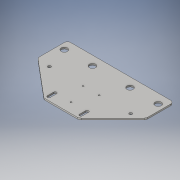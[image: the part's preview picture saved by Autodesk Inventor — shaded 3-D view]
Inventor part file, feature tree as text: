
AUTODESK INVENTOR PART (.ipt)
format: ipt  version: 2016 (Build 200138000, 138)  size: 213,504 bytes
history: native  units: in
note: dims shown in document units (in); Inventor stores cm internally (conversion verified against a paired STEP export)
features: sketch x7, extrude x4, hole x3
ambient origin geometry x8: Origin, YZ Plane, XZ Plane, XY Plane, X Axis, Y Axis, Z Axis, Center Point
bodies: Solid1 (feature_tree)
feature tree (14):
  extrude  "Extrusion1"  Depth=8.5in
  hole  "Hole1"  [1 undecoded]
  extrude  "Extrusion3"  Depth=3.1102in
  extrude  "Extrusion4"  Depth=0.25in
  extrude  "Extrusion5"  Depth=1.0236in
  hole  "Hole3"  [1 undecoded]
  hole  "Hole2"  [1 undecoded]
  sketch  "Sketch1"  dims[d0=8.5in d1=6.0in]
  sketch  "Sketch2"  dims[d2=0.125in d3=0.0in d4=5.6831in]
  sketch  "Sketch3"  dims[d5=1.0236in d7=3.1102in]
  sketch  "Sketch5"  dims[d12=0.2362in d13=0.75in d14=0.375in d15=0.25in d16=0.5635in d17=1.0in d18=0.8108in d19=1.0768in]
  sketch  "Sketch7"  dims[d20=3.1102in d21=1.0236in]
  sketch  "Sketch8"  dims[d22=3.124in d23=7.5728in]
  sketch  "Sketch10"  dims[d24=0.2953in d40=3.8881in d43=1.0in d44=0.0in d45=1.75in d47=1.75in d48=1.75in d49=1.75in d50=2.382in d52=2.5591in d53=0.6398in d54=0.6398in d55=2.382in d58=2.0472in d62=1.2795in d64=0.1181in d65=0.75in d66=0.375in d67=0.25in d68=0.5635in d69=1.0in d70=0.8108in d72=0.2362in d76=0.236in d77=0.492in d78=0.236in d79=0.492in d80=1.0in d81=0.0in d82=0.236in d83=0.492in d84=0.236in d85=0.492in d86=1.0in d87=0.0in d88=0.2362in d93=0.2953in d96=2.07in d99=135.0deg d100=0.25in d101=0.25in d102=0.25in d103=0.25in d104=0.962in d110=0.5in d111=2.25in d112=3.0in d113=2.25in d116=0.0007in d117=0.75in d118=0.5in d119=0.75in d120=0.375in d121=0.25in d122=0.5635in d123=1.0in d124=0.8108in d125=0.0in d126=2.5165in]
note: 3 required parameter values undecoded (feature->parameter linkage not recoverable at this tier; creation-order binding heuristic only, values carry confidence <= 0.55)
